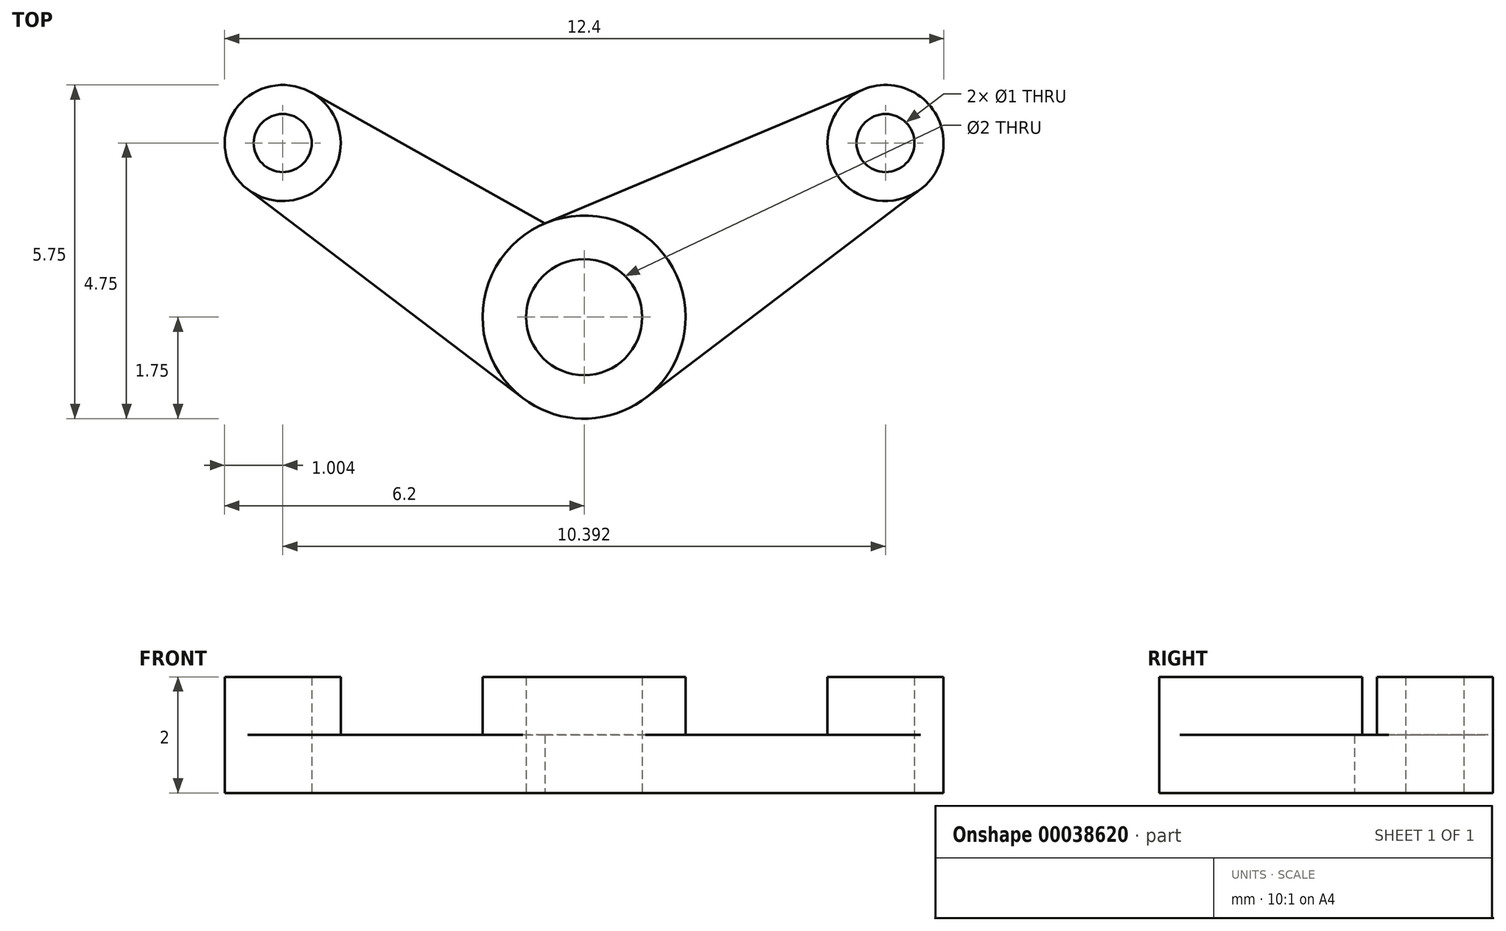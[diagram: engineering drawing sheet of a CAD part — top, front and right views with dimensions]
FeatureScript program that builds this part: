
annotation { "Feature Type Name" : "Feature", "Feature Type Description" : "" }
export const myFeature = defineFeature(function(context is Context, id is Id, definition is map)
    precondition{}
    {
        {
            var Q0;
            Q0=qCreatedBy(makeId("Top.planeOp"),FACE);
            var sketch = newSketch(context, id + "F0", { "sketchPlane" : qUnion([Q0])});
            skCircle(sketch, "E0", {"center": v(0, 0) * mm, "radius": 1 * mm});
            skCircle(sketch, "E1", {"center": v(0, 0) * mm, "radius": 1.75 * mm});
            skLineSegment(sketch, "E2", {"start": v(0, 0) * mm, "end": v(5.2, 0) * mm, "construction": true});
            skLineSegment(sketch, "E3", {"start": v(0, 0) * mm, "end": v(5.2, 3) * mm, "construction": true});
            skCircle(sketch, "E4", {"center": v(5.2, 3) * mm, "radius": 0.5 * mm});
            skCircle(sketch, "E5", {"center": v(5.2, 3) * mm, "radius": 1 * mm});
            skLineSegment(sketch, "E6", {"start": v(-0.68, 1.61) * mm, "end": v(4.8, 3.92) * mm});
            skLineSegment(sketch, "E7", {"start": v(1.06, -1.4) * mm, "end": v(5.8, 2.2) * mm});
            skLineSegment(sketch, "E8", {"start": v(0, 0) * mm, "end": v(-5.2, 0) * mm, "construction": true});
            skLineSegment(sketch, "E9", {"start": v(0, 0) * mm, "end": v(-5.2, 3) * mm, "construction": true});
            skCircle(sketch, "E10", {"center": v(-5.2, 3) * mm, "radius": 0.5 * mm});
            skCircle(sketch, "E11", {"center": v(-5.2, 3) * mm, "radius": 1 * mm});
            skLineSegment(sketch, "E12", {"start": v(-4.7, 3.87) * mm, "end": v(-0.68, 1.61) * mm});
            skLineSegment(sketch, "E13", {"start": v(-5.8, 2.2) * mm, "end": v(-1.06, -1.4) * mm});
            skSolve(sketch);
        }
        {
            var Q0;
            Q0=makeQuery(id+"F0.imprint","IMPRINT",FACE,{"disambiguationData":[TD([[makeQuery(id+"F0.imprint","IMPRINT",EDGE,{"derivedFrom":sQuery(id+"F0.wireOp",EDGE,"E0")}),-1.0]])]});
            var Q1;
            Q1=makeQuery(id+"F0.imprint","IMPRINT",FACE,{"disambiguationData":[TD([[makeQuery(id+"F0.imprint","IMPRINT",EDGE,{"derivedFrom":sQuery(id+"F0.wireOp",EDGE,"E4")}),-1.0]])]});
            extrude(context, id + "F1", {"entities" : qUnion([Q0, Q1]), "depth" : 2 * mm});
        }
        {
            var Q0;
            {var subQ1=sQuery(id+"F0.wireOp",EDGE,"E6");Q0=makeQuery(id+"F0.imprint","IMPRINT",FACE,{"disambiguationData":[TD([[makeQuery(id+"F0.imprint","IMPRINT",EDGE,{"derivedFrom":subQ1}),-1.0]])]});}
            extrude(context, id + "F2", {"entities" : qUnion([Q0]), "operationType" : NewBodyOperationType.ADD, "depth" : 1 * mm});
        }
        {
            var Q0;
            Q0=makeQuery(id+"F0.imprint","IMPRINT",FACE,{"disambiguationData":[TD([[makeQuery(id+"F0.imprint","IMPRINT",EDGE,{"derivedFrom":sQuery(id+"F0.wireOp",EDGE,"E10")}),-1.0]])]});
            extrude(context, id + "F3", {"entities" : qUnion([Q0]), "operationType" : NewBodyOperationType.ADD, "depth" : 2 * mm});
        }
        {
            var Q0;
            {var subQ1=sQuery(id+"F0.wireOp",EDGE,"E12");Q0=makeQuery(id+"F0.imprint","IMPRINT",FACE,{"disambiguationData":[TD([[makeQuery(id+"F0.imprint","IMPRINT",EDGE,{"derivedFrom":subQ1}),-1.0]])]});}
            extrude(context, id + "F4", {"entities" : qUnion([Q0]), "operationType" : NewBodyOperationType.ADD, "depth" : 1 * mm});
        }
    });
